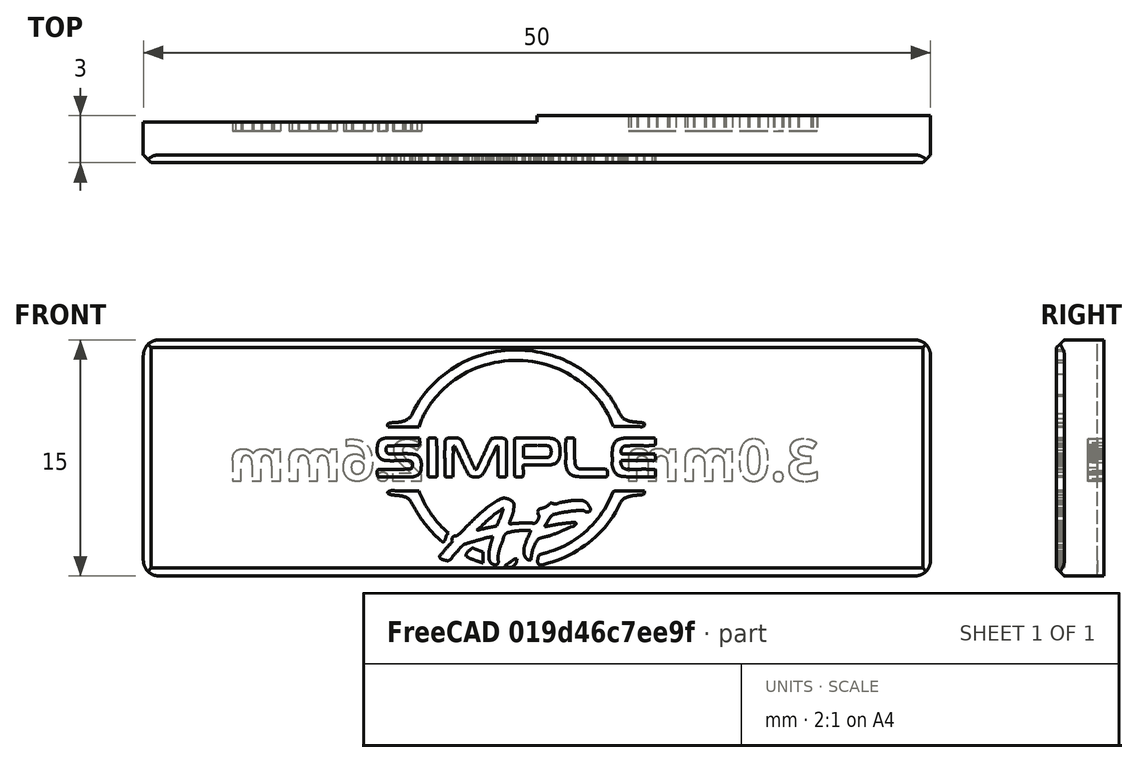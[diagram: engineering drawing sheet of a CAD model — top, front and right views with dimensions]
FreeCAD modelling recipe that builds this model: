
FCSTD DOCUMENT  (FreeCAD 26.3R20260630 (Git shallow))
Label: carto-measure
License: All rights reserved
LicenseURL: http://en.wikipedia.org/wiki/All_rights_reserved
objects: Sketcher::SketchObject×3, PartDesign::Pocket×2, App::Point×1, PartDesign::Pad×1, PartDesign::Chamfer×1, PartDesign::Fillet×1, PartDesign::Body×1
note: 22 computed .brp shape members not serialized (recipe doc carries the construction recipe); baked Part::Feature solids carry a one-line shape summary decoded from their .brp

FEATURE [App::Point] Origin001
  Role = Origin
FEATURE [Sketcher::SketchObject] Sketch
  ArcFitTolerance = 1e-06
  AttachmentSupport = -> [XY_Plane]
  ExternalTypes = [0]
  FullyConstrained = false
  MakeInternals = false
  MapMode = 5
  sketch-geometry (6):
    g0: LineSegment StartX=-28.082 StartY=2.6 StartZ=0 EndX=-3.08196 EndY=2.6 EndZ=0
    g1: LineSegment StartX=-3.08196 StartY=2.6 StartZ=0 EndX=-3.08196 EndY=3 EndZ=0
    g2: LineSegment StartX=-3.08196 StartY=3 StartZ=0 EndX=21.918 EndY=3 EndZ=0
    g3: LineSegment StartX=21.918 StartY=3 StartZ=0 EndX=21.918 EndY=0 EndZ=0
    g4: LineSegment StartX=21.918 StartY=0 StartZ=0 EndX=-28.082 EndY=0 EndZ=0
    g5: LineSegment StartX=-28.082 StartY=0 StartZ=0 EndX=-28.082 EndY=2.6 EndZ=0
  constraints (17):
    c: Horizontal(g0)
    c: Coincident(g0,g1)
    c: Vertical(g1)
    c: Coincident(g1,g2)
    c: Horizontal(g2)
    c: Coincident(g2,g3)
    c: PointOnObject(g3,g-1)
    c: Vertical(g3)
    c: Coincident(g3,g4)
    c: PointOnObject(g4,g-1)
    c: Coincident(g4,g5)
    c: Coincident(g5,g0)
    c: Vertical(g5)
    c: DistanceY(g5,g5) = 2.6
    c: DistanceY(g3,g3) = 3
    c: DistanceX(g4,g4) = 50
    c: DistanceX(g0,g0) = 25
FEATURE [PartDesign::Pad] Pad
  Direction = (0,0,1)
  FuzzyTolerance = 0
  Length = 15
  Length2 = 10
  Profile = -> Sketch
  ReferenceAxis = -> Sketch [N_Axis]
  SideType = 0
  Suppressed = false
  Type = 0
  Type2 = 0
FEATURE [Sketcher::SketchObject] Sketch001
  ArcFitTolerance = 1e-06
  AttachmentOffset = pos=(1,3.5,0) rot=(0,0,1;0rad)
  AttachmentSupport = -> [Pad]
  ExternalTypes = [0]
  FullyConstrained = false
  MakeInternals = true
  MapMode = 5
  Placement = pos=(1,8e-16,3.5) rot=(1,0,0;1.5708rad)
  sketch-geometry (160):
    g0: BSplineCurve PolesCount=4 KnotsCount=2 Degree=3 IsPeriodic=0
    g1: BSplineCurve PolesCount=4 KnotsCount=2 Degree=3 IsPeriodic=0
    g2: BSplineCurve PolesCount=4 KnotsCount=2 Degree=3 IsPeriodic=0
    g3: BSplineCurve PolesCount=4 KnotsCount=2 Degree=3 IsPeriodic=0
    g4: BSplineCurve PolesCount=4 KnotsCount=2 Degree=3 IsPeriodic=0
    g5: BSplineCurve PolesCount=4 KnotsCount=2 Degree=3 IsPeriodic=0
    g6: BSplineCurve PolesCount=4 KnotsCount=2 Degree=3 IsPeriodic=0
    g7: BSplineCurve PolesCount=4 KnotsCount=2 Degree=3 IsPeriodic=0
    g8: BSplineCurve PolesCount=4 KnotsCount=2 Degree=3 IsPeriodic=0
    g9: BSplineCurve PolesCount=4 KnotsCount=2 Degree=3 IsPeriodic=0
    g10: BSplineCurve PolesCount=4 KnotsCount=2 Degree=3 IsPeriodic=0
    g11: BSplineCurve PolesCount=4 KnotsCount=2 Degree=3 IsPeriodic=0
    g12: BSplineCurve PolesCount=4 KnotsCount=2 Degree=3 IsPeriodic=0
    g13: BSplineCurve PolesCount=4 KnotsCount=2 Degree=3 IsPeriodic=0
    g14: BSplineCurve PolesCount=4 KnotsCount=2 Degree=3 IsPeriodic=0
    g15: BSplineCurve PolesCount=4 KnotsCount=2 Degree=3 IsPeriodic=0
    g16: BSplineCurve PolesCount=4 KnotsCount=2 Degree=3 IsPeriodic=0
    g17: BSplineCurve PolesCount=4 KnotsCount=2 Degree=3 IsPeriodic=0
    g18: BSplineCurve PolesCount=4 KnotsCount=2 Degree=3 IsPeriodic=0
    g19: BSplineCurve PolesCount=4 KnotsCount=2 Degree=3 IsPeriodic=0
    g20: BSplineCurve PolesCount=4 KnotsCount=2 Degree=3 IsPeriodic=0
    g21: BSplineCurve PolesCount=4 KnotsCount=2 Degree=3 IsPeriodic=0
    g22: BSplineCurve PolesCount=4 KnotsCount=2 Degree=3 IsPeriodic=0
    g23: BSplineCurve PolesCount=4 KnotsCount=2 Degree=3 IsPeriodic=0
    g24: BSplineCurve PolesCount=4 KnotsCount=2 Degree=3 IsPeriodic=0
    g25: BSplineCurve PolesCount=4 KnotsCount=2 Degree=3 IsPeriodic=0
    g26: BSplineCurve PolesCount=4 KnotsCount=2 Degree=3 IsPeriodic=0
    g27: BSplineCurve PolesCount=4 KnotsCount=2 Degree=3 IsPeriodic=0
    g28: BSplineCurve PolesCount=4 KnotsCount=2 Degree=3 IsPeriodic=0
    g29: BSplineCurve PolesCount=4 KnotsCount=2 Degree=3 IsPeriodic=0
    g30: BSplineCurve PolesCount=4 KnotsCount=2 Degree=3 IsPeriodic=0
    g31: BSplineCurve PolesCount=4 KnotsCount=2 Degree=3 IsPeriodic=0
    g32: BSplineCurve PolesCount=4 KnotsCount=2 Degree=3 IsPeriodic=0
    g33: BSplineCurve PolesCount=4 KnotsCount=2 Degree=3 IsPeriodic=0
    g34: BSplineCurve PolesCount=4 KnotsCount=2 Degree=3 IsPeriodic=0
    g35: BSplineCurve PolesCount=4 KnotsCount=2 Degree=3 IsPeriodic=0
    g36: BSplineCurve PolesCount=4 KnotsCount=2 Degree=3 IsPeriodic=0
    g37: BSplineCurve PolesCount=4 KnotsCount=2 Degree=3 IsPeriodic=0
    g38: BSplineCurve PolesCount=4 KnotsCount=2 Degree=3 IsPeriodic=0
    g39: BSplineCurve PolesCount=4 KnotsCount=2 Degree=3 IsPeriodic=0
    g40: BSplineCurve PolesCount=4 KnotsCount=2 Degree=3 IsPeriodic=0
    g41: BSplineCurve PolesCount=4 KnotsCount=2 Degree=3 IsPeriodic=0
    g42: BSplineCurve PolesCount=4 KnotsCount=2 Degree=3 IsPeriodic=0
    g43: BSplineCurve PolesCount=4 KnotsCount=2 Degree=3 IsPeriodic=0
    g44: BSplineCurve PolesCount=4 KnotsCount=2 Degree=3 IsPeriodic=0
    g45: BSplineCurve PolesCount=4 KnotsCount=2 Degree=3 IsPeriodic=0
    g46: BSplineCurve PolesCount=4 KnotsCount=2 Degree=3 IsPeriodic=0
    g47: BSplineCurve PolesCount=4 KnotsCount=2 Degree=3 IsPeriodic=0
    g48: BSplineCurve PolesCount=4 KnotsCount=2 Degree=3 IsPeriodic=0
    g49: BSplineCurve PolesCount=4 KnotsCount=2 Degree=3 IsPeriodic=0
    g50: BSplineCurve PolesCount=4 KnotsCount=2 Degree=3 IsPeriodic=0
    g51: BSplineCurve PolesCount=4 KnotsCount=2 Degree=3 IsPeriodic=0
    g52: BSplineCurve PolesCount=4 KnotsCount=2 Degree=3 IsPeriodic=0
    g53: BSplineCurve PolesCount=4 KnotsCount=2 Degree=3 IsPeriodic=0
    g54: BSplineCurve PolesCount=4 KnotsCount=2 Degree=3 IsPeriodic=0
    g55: BSplineCurve PolesCount=4 KnotsCount=2 Degree=3 IsPeriodic=0
    g56: BSplineCurve PolesCount=4 KnotsCount=2 Degree=3 IsPeriodic=0
    g57: BSplineCurve PolesCount=4 KnotsCount=2 Degree=3 IsPeriodic=0
    g58: BSplineCurve PolesCount=4 KnotsCount=2 Degree=3 IsPeriodic=0
    g59: BSplineCurve PolesCount=4 KnotsCount=2 Degree=3 IsPeriodic=0
    g60: BSplineCurve PolesCount=4 KnotsCount=2 Degree=3 IsPeriodic=0
    g61: BSplineCurve PolesCount=4 KnotsCount=2 Degree=3 IsPeriodic=0
    g62: BSplineCurve PolesCount=4 KnotsCount=2 Degree=3 IsPeriodic=0
    g63: BSplineCurve PolesCount=4 KnotsCount=2 Degree=3 IsPeriodic=0
    g64: BSplineCurve PolesCount=4 KnotsCount=2 Degree=3 IsPeriodic=0
    g65: BSplineCurve PolesCount=4 KnotsCount=2 Degree=3 IsPeriodic=0
    g66: BSplineCurve PolesCount=4 KnotsCount=2 Degree=3 IsPeriodic=0
    g67: BSplineCurve PolesCount=4 KnotsCount=2 Degree=3 IsPeriodic=0
    g68: BSplineCurve PolesCount=4 KnotsCount=2 Degree=3 IsPeriodic=0
    g69: BSplineCurve PolesCount=4 KnotsCount=2 Degree=3 IsPeriodic=0
    g70: BSplineCurve PolesCount=4 KnotsCount=2 Degree=3 IsPeriodic=0
    g71: BSplineCurve PolesCount=4 KnotsCount=2 Degree=3 IsPeriodic=0
    g72: BSplineCurve PolesCount=4 KnotsCount=2 Degree=3 IsPeriodic=0
    g73: BSplineCurve PolesCount=4 KnotsCount=2 Degree=3 IsPeriodic=0
    g74: BSplineCurve PolesCount=4 KnotsCount=2 Degree=3 IsPeriodic=0
    g75: BSplineCurve PolesCount=4 KnotsCount=2 Degree=3 IsPeriodic=0
    g76: BSplineCurve PolesCount=4 KnotsCount=2 Degree=3 IsPeriodic=0
    g77: BSplineCurve PolesCount=4 KnotsCount=2 Degree=3 IsPeriodic=0
    g78: BSplineCurve PolesCount=4 KnotsCount=2 Degree=3 IsPeriodic=0
    g79: BSplineCurve PolesCount=4 KnotsCount=2 Degree=3 IsPeriodic=0
    g80: BSplineCurve PolesCount=4 KnotsCount=2 Degree=3 IsPeriodic=0
    g81: BSplineCurve PolesCount=4 KnotsCount=2 Degree=3 IsPeriodic=0
    g82: BSplineCurve PolesCount=4 KnotsCount=2 Degree=3 IsPeriodic=0
    g83: BSplineCurve PolesCount=4 KnotsCount=2 Degree=3 IsPeriodic=0
    g84: BSplineCurve PolesCount=4 KnotsCount=2 Degree=3 IsPeriodic=0
    g85: BSplineCurve PolesCount=4 KnotsCount=2 Degree=3 IsPeriodic=0
    g86: BSplineCurve PolesCount=4 KnotsCount=2 Degree=3 IsPeriodic=0
    g87: BSplineCurve PolesCount=4 KnotsCount=2 Degree=3 IsPeriodic=0
    g88: BSplineCurve PolesCount=4 KnotsCount=2 Degree=3 IsPeriodic=0
    g89: BSplineCurve PolesCount=4 KnotsCount=2 Degree=3 IsPeriodic=0
    g90: BSplineCurve PolesCount=4 KnotsCount=2 Degree=3 IsPeriodic=0
    g91: BSplineCurve PolesCount=4 KnotsCount=2 Degree=3 IsPeriodic=0
    g92: BSplineCurve PolesCount=4 KnotsCount=2 Degree=3 IsPeriodic=0
    g93: BSplineCurve PolesCount=4 KnotsCount=2 Degree=3 IsPeriodic=0
    g94: BSplineCurve PolesCount=4 KnotsCount=2 Degree=3 IsPeriodic=0
    g95: BSplineCurve PolesCount=4 KnotsCount=2 Degree=3 IsPeriodic=0
    g96: BSplineCurve PolesCount=4 KnotsCount=2 Degree=3 IsPeriodic=0
    g97: BSplineCurve PolesCount=4 KnotsCount=2 Degree=3 IsPeriodic=0
    g98: BSplineCurve PolesCount=4 KnotsCount=2 Degree=3 IsPeriodic=0
    g99: BSplineCurve PolesCount=4 KnotsCount=2 Degree=3 IsPeriodic=0
    g100: BSplineCurve PolesCount=4 KnotsCount=2 Degree=3 IsPeriodic=0
    g101: BSplineCurve PolesCount=4 KnotsCount=2 Degree=3 IsPeriodic=0
    g102: BSplineCurve PolesCount=4 KnotsCount=2 Degree=3 IsPeriodic=0
    g103: BSplineCurve PolesCount=4 KnotsCount=2 Degree=3 IsPeriodic=0
    g104: BSplineCurve PolesCount=4 KnotsCount=2 Degree=3 IsPeriodic=0
    g105: BSplineCurve PolesCount=2 KnotsCount=2 Degree=1 IsPeriodic=0
    g106: BSplineCurve PolesCount=4 KnotsCount=2 Degree=3 IsPeriodic=0
    g107: BSplineCurve PolesCount=4 KnotsCount=2 Degree=3 IsPeriodic=0
    g108: BSplineCurve PolesCount=4 KnotsCount=2 Degree=3 IsPeriodic=0
    g109: BSplineCurve PolesCount=4 KnotsCount=2 Degree=3 IsPeriodic=0
    g110: BSplineCurve PolesCount=4 KnotsCount=2 Degree=3 IsPeriodic=0
    g111: BSplineCurve PolesCount=4 KnotsCount=2 Degree=3 IsPeriodic=0
    g112: BSplineCurve PolesCount=4 KnotsCount=2 Degree=3 IsPeriodic=0
    g113: BSplineCurve PolesCount=4 KnotsCount=2 Degree=3 IsPeriodic=0
    g114: BSplineCurve PolesCount=4 KnotsCount=2 Degree=3 IsPeriodic=0
    g115: BSplineCurve PolesCount=4 KnotsCount=2 Degree=3 IsPeriodic=0
    g116: BSplineCurve PolesCount=4 KnotsCount=2 Degree=3 IsPeriodic=0
    g117: BSplineCurve PolesCount=4 KnotsCount=2 Degree=3 IsPeriodic=0
    g118: BSplineCurve PolesCount=4 KnotsCount=2 Degree=3 IsPeriodic=0
    g119: BSplineCurve PolesCount=4 KnotsCount=2 Degree=3 IsPeriodic=0
    g120: BSplineCurve PolesCount=4 KnotsCount=2 Degree=3 IsPeriodic=0
    g121: BSplineCurve PolesCount=4 KnotsCount=2 Degree=3 IsPeriodic=0
    g122: BSplineCurve PolesCount=4 KnotsCount=2 Degree=3 IsPeriodic=0
    g123: BSplineCurve PolesCount=4 KnotsCount=2 Degree=3 IsPeriodic=0
    g124: BSplineCurve PolesCount=4 KnotsCount=2 Degree=3 IsPeriodic=0
    g125: BSplineCurve PolesCount=4 KnotsCount=2 Degree=3 IsPeriodic=0
    g126: BSplineCurve PolesCount=4 KnotsCount=2 Degree=3 IsPeriodic=0
    g127: BSplineCurve PolesCount=4 KnotsCount=2 Degree=3 IsPeriodic=0
    g128: BSplineCurve PolesCount=4 KnotsCount=2 Degree=3 IsPeriodic=0
    g129: BSplineCurve PolesCount=4 KnotsCount=2 Degree=3 IsPeriodic=0
    g130: BSplineCurve PolesCount=4 KnotsCount=2 Degree=3 IsPeriodic=0
    g131: BSplineCurve PolesCount=4 KnotsCount=2 Degree=3 IsPeriodic=0
    g132: BSplineCurve PolesCount=4 KnotsCount=2 Degree=3 IsPeriodic=0
    g133: BSplineCurve PolesCount=4 KnotsCount=2 Degree=3 IsPeriodic=0
    g134: BSplineCurve PolesCount=4 KnotsCount=2 Degree=3 IsPeriodic=0
    g135: BSplineCurve PolesCount=4 KnotsCount=2 Degree=3 IsPeriodic=0
    g136: BSplineCurve PolesCount=4 KnotsCount=2 Degree=3 IsPeriodic=0
    g137: BSplineCurve PolesCount=4 KnotsCount=2 Degree=3 IsPeriodic=0
    g138: BSplineCurve PolesCount=4 KnotsCount=2 Degree=3 IsPeriodic=0
    g139: BSplineCurve PolesCount=4 KnotsCount=2 Degree=3 IsPeriodic=0
    g140: BSplineCurve PolesCount=4 KnotsCount=2 Degree=3 IsPeriodic=0
    g141: BSplineCurve PolesCount=4 KnotsCount=2 Degree=3 IsPeriodic=0
    g142: BSplineCurve PolesCount=4 KnotsCount=2 Degree=3 IsPeriodic=0
    g143: BSplineCurve PolesCount=4 KnotsCount=2 Degree=3 IsPeriodic=0
    g144: BSplineCurve PolesCount=4 KnotsCount=2 Degree=3 IsPeriodic=0
    g145: BSplineCurve PolesCount=4 KnotsCount=2 Degree=3 IsPeriodic=0
    g146: BSplineCurve PolesCount=4 KnotsCount=2 Degree=3 IsPeriodic=0
    g147: BSplineCurve PolesCount=4 KnotsCount=2 Degree=3 IsPeriodic=0
    g148: BSplineCurve PolesCount=4 KnotsCount=2 Degree=3 IsPeriodic=0
    g149: BSplineCurve PolesCount=4 KnotsCount=2 Degree=3 IsPeriodic=0
    g150: BSplineCurve PolesCount=4 KnotsCount=2 Degree=3 IsPeriodic=0
    g151: BSplineCurve PolesCount=4 KnotsCount=2 Degree=3 IsPeriodic=0
    g152: BSplineCurve PolesCount=4 KnotsCount=2 Degree=3 IsPeriodic=0
    g153: BSplineCurve PolesCount=4 KnotsCount=2 Degree=3 IsPeriodic=0
    g154: BSplineCurve PolesCount=4 KnotsCount=2 Degree=3 IsPeriodic=0
    g155: BSplineCurve PolesCount=4 KnotsCount=2 Degree=3 IsPeriodic=0
    g156: BSplineCurve PolesCount=4 KnotsCount=2 Degree=3 IsPeriodic=0
    g157: BSplineCurve PolesCount=4 KnotsCount=2 Degree=3 IsPeriodic=0
    g158: BSplineCurve PolesCount=4 KnotsCount=2 Degree=3 IsPeriodic=0
    g159: BSplineCurve PolesCount=4 KnotsCount=2 Degree=3 IsPeriodic=0
  constraints (160):
    c: Coincident(g117,g118)
    c: Coincident(g118,g119)
    c: Coincident(g108,g109)
    c: Coincident(g107,g108)
    c: Coincident(g112,g113)
    c: Coincident(g7,g8)
    c: Coincident(g156,g157)
    c: Coincident(g113,g114)
    c: Coincident(g8,g9)
    c: Coincident(g157,g158)
    c: Coincident(g109,g110)
    c: Coincident(g116,g117)
    c: Coincident(g106,g107)
    c: Coincident(g155,g156)
    c: Coincident(g119,g120)
    c: Coincident(g106,g120)
    c: Coincident(g9,g10)
    c: Coincident(g114,g115)
    c: Coincident(g158,g159)
    c: Coincident(g6,g7)
    c: Coincident(g111,g112)
    c: Coincident(g110,g111)
    c: Coincident(g115,g116)
    c: Coincident(g102,g103)
    c: Coincident(g101,g102)
    c: Coincident(g101,g105)
    c: Coincident(g154,g155)
    c: Coincident(g103,g104)
    c: Coincident(g104,g105)
    c: Coincident(g5,g6)
    c: Coincident(g61,g62)
    c: Coincident(g153,g154)
    c: Coincident(g94,g95)
    c: Coincident(g95,g96)
    c: Coincident(g62,g63)
    c: Coincident(g153,g159)
    c: Coincident(g93,g94)
    c: Coincident(g60,g61)
    c: Coincident(g92,g93)
    c: Coincident(g91,g92)
    c: Coincident(g63,g64)
    c: Coincident(g59,g60)
    c: Coincident(g96,g97)
    c: Coincident(g64,g65)
    c: Coincident(g65,g66)
    c: Coincident(g143,g144)
    c: Coincident(g97,g98)
    c: Coincident(g58,g59)
    c: Coincident(g90,g91)
    c: Coincident(g141,g144)
    c: Coincident(g98,g99)
    c: Coincident(g125,g126)
    c: Coincident(g121,g126)
    c: Coincident(g99,g100)
    c: Coincident(g89,g90)
    c: Coincident(g141,g142)
    c: Coincident(g82,g100)
    c: Coincident(g142,g143)
    c: Coincident(g66,g67)
    c: Coincident(g124,g125)
    c: Coincident(g69,g70)
    c: Coincident(g68,g69)
    c: Coincident(g82,g83)
    c: Coincident(g67,g68)
    c: Coincident(g88,g89)
    c: Coincident(g123,g124)
    c: Coincident(g121,g122)
    c: Coincident(g87,g88)
    c: Coincident(g86,g87)
    c: Coincident(g70,g71)
    c: Coincident(g57,g58)
    c: Coincident(g71,g72)
    c: Coincident(g10,g11)
    c: Coincident(g31,g72)
    c: Coincident(g122,g123)
    c: Coincident(g83,g84)
    c: Coincident(g84,g85)
    c: Coincident(g85,g86)
    c: Coincident(g27,g28)
    c: Coincident(g28,g29)
    c: Coincident(g31,g32)
    c: Coincident(g53,g54)
    c: Coincident(g56,g57)
    c: Coincident(g54,g55)
    c: Coincident(g52,g53)
    c: Coincident(g55,g56)
    c: Coincident(g78,g79)
    c: Coincident(g77,g78)
    c: Coincident(g27,g30)
    c: Coincident(g29,g30)
    c: Coincident(g76,g77)
    c: Coincident(g75,g76)
    c: Coincident(g128,g129)
    c: Coincident(g127,g128)
    c: Coincident(g33,g34)
    c: Coincident(g34,g35)
    c: Coincident(g79,g80)
    c: Coincident(g32,g33)
    c: Coincident(g35,g36)
    c: Coincident(g51,g52)
    c: Coincident(g127,g131)
    c: Coincident(g4,g5)
    c: Coincident(g36,g37)
    c: Coincident(g145,g152)
    c: Coincident(g50,g51)
    c: Coincident(g74,g75)
    c: Coincident(g151,g152)
    c: Coincident(g49,g50)
    c: Coincident(g41,g42)
    c: Coincident(g129,g130)
    c: Coincident(g130,g131)
    c: Coincident(g145,g146)
    c: Coincident(g48,g49)
    c: Coincident(g42,g43)
    c: Coincident(g80,g81)
    c: Coincident(g37,g38)
    c: Coincident(g73,g81)
    c: Coincident(g73,g74)
    c: Coincident(g47,g48)
    c: Coincident(g135,g136)
    c: Coincident(g136,g137)
    c: Coincident(g38,g39)
    c: Coincident(g39,g40)
    c: Coincident(g40,g41)
    c: Coincident(g134,g135)
    c: Coincident(g137,g138)
    c: Coincident(g138,g139)
    c: Coincident(g46,g47)
    c: Coincident(g43,g44)
    c: Coincident(g11,g12)
    c: Coincident(g45,g46)
    c: Coincident(g44,g45)
    c: Coincident(g139,g140)
    c: Coincident(g132,g140)
    c: Coincident(g133,g134)
    c: Coincident(g132,g133)
    c: Coincident(g0,g12)
    c: Coincident(g24,g25)
    c: Coincident(g146,g147)
    c: Coincident(g3,g4)
    c: Coincident(g25,g26)
    c: Coincident(g150,g151)
    c: Coincident(g19,g20)
    c: Coincident(g16,g17)
    c: Coincident(g23,g24)
    c: Coincident(g0,g1)
    c: Coincident(g15,g16)
    c: Coincident(g13,g26)
    c: Coincident(g147,g148)
    c: Coincident(g20,g21)
    c: Coincident(g2,g3)
    c: Coincident(g149,g150)
    c: Coincident(g1,g2)
    c: Coincident(g148,g149)
    c: Coincident(g18,g19)
    c: Coincident(g22,g23)
    c: Coincident(g14,g15)
    c: Coincident(g17,g18)
    c: Coincident(g21,g22)
    c: Coincident(g13,g14)
FEATURE [PartDesign::Pocket] Pocket
  BaseFeature = -> Pad
  Direction = (0,1,-2e-16)
  FuzzyTolerance = 0
  Length = 0.5
  Length2 = 5
  Profile = -> Sketch001
  ReferenceAxis = -> Sketch001 [N_Axis]
  Refine = true
  SideType = 0
  Suppressed = false
  Type = 0
  Type2 = 0
FEATURE [PartDesign::Chamfer] Chamfer
  Angle = 45
  Base = -> Pocket [Edge13,Edge16,Edge17,Edge5]
  BaseFeature = -> Pocket
  ChamferType = 0
  FlipDirection = false
  FuzzyTolerance = 0
  Refine = true
  Size = 0.5
  Size2 = 1
  SupportTransform = false
  Suppressed = false
  UseAllEdges = false
FEATURE [PartDesign::Fillet] Fillet
  Base = -> Chamfer [Edge5,Edge1,Edge4,Edge15]
  BaseFeature = -> Chamfer
  FuzzyTolerance = 0
  Radius = 1
  Refine = true
  SupportTransform = false
  Suppressed = false
  UseAllEdges = false
FEATURE [Sketcher::SketchObject] Sketch002
  ArcFitTolerance = 1e-06
  AttachmentSupport = -> [Fillet]
  ExternalTypes = [0]
  FullyConstrained = false
  MakeInternals = true
  MapMode = 5
  Placement = pos=(0,3,0) rot=(0,0.707107,0.707107;3.14159rad)
  sketch-geometry (222):
    g0: LineSegment [constr] StartX=-14.7202 StartY=6 StartZ=0 EndX=-2.72016 EndY=6 EndZ=0
    g1: LineSegment [constr] StartX=10.4105 StartY=6 StartZ=0 EndX=22.4105 EndY=6 EndZ=0
    g2: BSplineCurve PolesCount=3 KnotsCount=2 Degree=2 IsPeriodic=0
    g3: BSplineCurve PolesCount=3 KnotsCount=2 Degree=2 IsPeriodic=0
    g4: LineSegment StartX=-13.5529 StartY=7.4247 StartZ=0 EndX=-13.5529 EndY=7.41397 EndZ=0
    g5: BSplineCurve PolesCount=3 KnotsCount=2 Degree=2 IsPeriodic=0
    g6: BSplineCurve PolesCount=3 KnotsCount=2 Degree=2 IsPeriodic=0
    g7: BSplineCurve PolesCount=3 KnotsCount=2 Degree=2 IsPeriodic=0
    g8: BSplineCurve PolesCount=3 KnotsCount=2 Degree=2 IsPeriodic=0
    g9: BSplineCurve PolesCount=3 KnotsCount=2 Degree=2 IsPeriodic=0
    g10: LineSegment StartX=-14.7202 StartY=6.15373 StartZ=0 EndX=-14.7202 EndY=6.62386 EndZ=0
    g11: BSplineCurve PolesCount=3 KnotsCount=2 Degree=2 IsPeriodic=0
    g12: BSplineCurve PolesCount=3 KnotsCount=2 Degree=2 IsPeriodic=0
    g13: BSplineCurve PolesCount=3 KnotsCount=2 Degree=2 IsPeriodic=0
    g14: BSplineCurve PolesCount=3 KnotsCount=2 Degree=2 IsPeriodic=0
    g15: BSplineCurve PolesCount=3 KnotsCount=2 Degree=2 IsPeriodic=0
    g16: BSplineCurve PolesCount=3 KnotsCount=2 Degree=2 IsPeriodic=0
    g17: LineSegment StartX=-14.1195 StartY=7.1798 StartZ=0 EndX=-14.318 EndY=7.1798 EndZ=0
    g18: LineSegment StartX=-14.318 StartY=7.1798 StartZ=0 EndX=-14.318 EndY=7.60346 EndZ=0
    g19: LineSegment StartX=-14.318 StartY=7.60346 StartZ=0 EndX=-14.116 EndY=7.60346 EndZ=0
    g20: BSplineCurve PolesCount=3 KnotsCount=2 Degree=2 IsPeriodic=0
    g21: BSplineCurve PolesCount=3 KnotsCount=2 Degree=2 IsPeriodic=0
    g22: BSplineCurve PolesCount=3 KnotsCount=2 Degree=2 IsPeriodic=0
    g23: BSplineCurve PolesCount=3 KnotsCount=2 Degree=2 IsPeriodic=0
    g24: BSplineCurve PolesCount=3 KnotsCount=2 Degree=2 IsPeriodic=0
    g25: LineSegment StartX=-14.461 StartY=8.06108 StartZ=0 EndX=-14.7166 EndY=8.44183 EndZ=0
    g26: BSplineCurve PolesCount=3 KnotsCount=2 Degree=2 IsPeriodic=0
    g27: BSplineCurve PolesCount=3 KnotsCount=2 Degree=2 IsPeriodic=0
    g28: BSplineCurve PolesCount=3 KnotsCount=2 Degree=2 IsPeriodic=0
    g29: BSplineCurve PolesCount=3 KnotsCount=2 Degree=2 IsPeriodic=0
    g30: BSplineCurve PolesCount=3 KnotsCount=2 Degree=2 IsPeriodic=0
    g31: BSplineCurve PolesCount=3 KnotsCount=2 Degree=2 IsPeriodic=0
    g32: BSplineCurve PolesCount=3 KnotsCount=2 Degree=2 IsPeriodic=0
    g33: BSplineCurve PolesCount=3 KnotsCount=2 Degree=2 IsPeriodic=0
    g34: BSplineCurve PolesCount=3 KnotsCount=2 Degree=2 IsPeriodic=0
    g35: BSplineCurve PolesCount=3 KnotsCount=2 Degree=2 IsPeriodic=0
    g36: BSplineCurve PolesCount=3 KnotsCount=2 Degree=2 IsPeriodic=0
    g37: BSplineCurve PolesCount=3 KnotsCount=2 Degree=2 IsPeriodic=0
    g38: BSplineCurve PolesCount=3 KnotsCount=2 Degree=2 IsPeriodic=0
    g39: BSplineCurve PolesCount=3 KnotsCount=2 Degree=2 IsPeriodic=0
    g40: BSplineCurve PolesCount=3 KnotsCount=2 Degree=2 IsPeriodic=0
    g41: BSplineCurve PolesCount=3 KnotsCount=2 Degree=2 IsPeriodic=0
    g42: BSplineCurve PolesCount=3 KnotsCount=2 Degree=2 IsPeriodic=0
    g43: BSplineCurve PolesCount=3 KnotsCount=2 Degree=2 IsPeriodic=0
    g44: BSplineCurve PolesCount=3 KnotsCount=2 Degree=2 IsPeriodic=0
    g45: BSplineCurve PolesCount=3 KnotsCount=2 Degree=2 IsPeriodic=0
    g46: BSplineCurve PolesCount=3 KnotsCount=2 Degree=2 IsPeriodic=0
    g47: BSplineCurve PolesCount=3 KnotsCount=2 Degree=2 IsPeriodic=0
    g48: BSplineCurve PolesCount=3 KnotsCount=2 Degree=2 IsPeriodic=0
    g49: BSplineCurve PolesCount=3 KnotsCount=2 Degree=2 IsPeriodic=0
    g50: BSplineCurve PolesCount=3 KnotsCount=2 Degree=2 IsPeriodic=0
    g51: BSplineCurve PolesCount=3 KnotsCount=2 Degree=2 IsPeriodic=0
    g52: BSplineCurve PolesCount=3 KnotsCount=2 Degree=2 IsPeriodic=0
    g53: LineSegment StartX=-7.56092 StartY=6.04826 StartZ=0 EndX=-8.10613 EndY=6.04826 EndZ=0
    g54: LineSegment StartX=-8.10613 StartY=6.04826 StartZ=0 EndX=-8.10613 EndY=7.21555 EndZ=0
    g55: BSplineCurve PolesCount=3 KnotsCount=2 Degree=2 IsPeriodic=0
    g56: BSplineCurve PolesCount=3 KnotsCount=2 Degree=2 IsPeriodic=0
    g57: BSplineCurve PolesCount=3 KnotsCount=2 Degree=2 IsPeriodic=0
    g58: BSplineCurve PolesCount=3 KnotsCount=2 Degree=2 IsPeriodic=0
    g59: LineSegment StartX=-8.80507 StartY=6.98853 StartZ=0 EndX=-8.80507 EndY=6.04826 EndZ=0
    g60: LineSegment StartX=-8.80507 StartY=6.04826 StartZ=0 EndX=-9.35028 EndY=6.04826 EndZ=0
    g61: LineSegment StartX=-9.35028 StartY=6.04826 StartZ=0 EndX=-9.35028 EndY=8.04678 EndZ=0
    g62: LineSegment StartX=-9.35028 StartY=8.04678 StartZ=0 EndX=-8.93378 EndY=8.04678 EndZ=0
    g63: LineSegment StartX=-8.93378 StartY=8.04678 StartZ=0 EndX=-8.86048 EndY=7.79115 EndZ=0
    g64: LineSegment StartX=-8.86048 StartY=7.79115 StartZ=0 EndX=-8.8301 EndY=7.79115 EndZ=0
    g65: BSplineCurve PolesCount=3 KnotsCount=2 Degree=2 IsPeriodic=0
    g66: BSplineCurve PolesCount=3 KnotsCount=2 Degree=2 IsPeriodic=0
    g67: BSplineCurve PolesCount=3 KnotsCount=2 Degree=2 IsPeriodic=0
    g68: LineSegment StartX=-7.64136 StartY=7.79115 StartZ=0 EndX=-7.59309 EndY=7.79115 EndZ=0
    g69: BSplineCurve PolesCount=3 KnotsCount=2 Degree=2 IsPeriodic=0
    g70: BSplineCurve PolesCount=3 KnotsCount=2 Degree=2 IsPeriodic=0
    g71: BSplineCurve PolesCount=3 KnotsCount=2 Degree=2 IsPeriodic=0
    g72: BSplineCurve PolesCount=3 KnotsCount=2 Degree=2 IsPeriodic=0
    g73: LineSegment StartX=-6.31498 StartY=7.35141 StartZ=0 EndX=-6.31498 EndY=6.04826 EndZ=0
    g74: LineSegment StartX=-6.31498 StartY=6.04826 StartZ=0 EndX=-6.86197 EndY=6.04826 EndZ=0
    g75: LineSegment StartX=-6.86197 StartY=6.04826 StartZ=0 EndX=-6.86197 EndY=7.21555 EndZ=0
    g76: BSplineCurve PolesCount=3 KnotsCount=2 Degree=2 IsPeriodic=0
    g77: BSplineCurve PolesCount=3 KnotsCount=2 Degree=2 IsPeriodic=0
    g78: BSplineCurve PolesCount=3 KnotsCount=2 Degree=2 IsPeriodic=0
    g79: BSplineCurve PolesCount=3 KnotsCount=2 Degree=2 IsPeriodic=0
    g80: LineSegment StartX=-7.56092 StartY=7.0511 StartZ=0 EndX=-7.56092 EndY=6.04826 EndZ=0
    g81: LineSegment StartX=-3.9661 StartY=6.04826 StartZ=0 EndX=-4.51131 EndY=6.04826 EndZ=0
    g82: LineSegment StartX=-4.51131 StartY=6.04826 StartZ=0 EndX=-4.51131 EndY=7.21555 EndZ=0
    g83: BSplineCurve PolesCount=3 KnotsCount=2 Degree=2 IsPeriodic=0
    g84: BSplineCurve PolesCount=3 KnotsCount=2 Degree=2 IsPeriodic=0
    g85: BSplineCurve PolesCount=3 KnotsCount=2 Degree=2 IsPeriodic=0
    g86: BSplineCurve PolesCount=3 KnotsCount=2 Degree=2 IsPeriodic=0
    g87: LineSegment StartX=-5.21025 StartY=6.98853 StartZ=0 EndX=-5.21025 EndY=6.04826 EndZ=0
    g88: LineSegment StartX=-5.21025 StartY=6.04826 StartZ=0 EndX=-5.75546 EndY=6.04826 EndZ=0
    g89: LineSegment StartX=-5.75546 StartY=6.04826 StartZ=0 EndX=-5.75546 EndY=8.04678 EndZ=0
    g90: LineSegment StartX=-5.75546 StartY=8.04678 StartZ=0 EndX=-5.33896 EndY=8.04678 EndZ=0
    g91: LineSegment StartX=-5.33896 StartY=8.04678 StartZ=0 EndX=-5.26567 EndY=7.79115 EndZ=0
    g92: LineSegment StartX=-5.26567 StartY=7.79115 StartZ=0 EndX=-5.23528 EndY=7.79115 EndZ=0
    g93: BSplineCurve PolesCount=3 KnotsCount=2 Degree=2 IsPeriodic=0
    g94: BSplineCurve PolesCount=3 KnotsCount=2 Degree=2 IsPeriodic=0
    g95: BSplineCurve PolesCount=3 KnotsCount=2 Degree=2 IsPeriodic=0
    g96: LineSegment StartX=-4.04654 StartY=7.79115 StartZ=0 EndX=-3.99828 EndY=7.79115 EndZ=0
    g97: BSplineCurve PolesCount=3 KnotsCount=2 Degree=2 IsPeriodic=0
    g98: BSplineCurve PolesCount=3 KnotsCount=2 Degree=2 IsPeriodic=0
    g99: BSplineCurve PolesCount=3 KnotsCount=2 Degree=2 IsPeriodic=0
    g100: BSplineCurve PolesCount=3 KnotsCount=2 Degree=2 IsPeriodic=0
    g101: LineSegment StartX=-2.72016 StartY=7.35141 StartZ=0 EndX=-2.72016 EndY=6.04826 EndZ=0
    g102: LineSegment StartX=-2.72016 StartY=6.04826 StartZ=0 EndX=-3.26716 EndY=6.04826 EndZ=0
    g103: LineSegment StartX=-3.26716 StartY=6.04826 StartZ=0 EndX=-3.26716 EndY=7.21555 EndZ=0
    g104: BSplineCurve PolesCount=3 KnotsCount=2 Degree=2 IsPeriodic=0
    g105: BSplineCurve PolesCount=3 KnotsCount=2 Degree=2 IsPeriodic=0
    g106: BSplineCurve PolesCount=3 KnotsCount=2 Degree=2 IsPeriodic=0
    g107: BSplineCurve PolesCount=3 KnotsCount=2 Degree=2 IsPeriodic=0
    g108: LineSegment StartX=-3.9661 StartY=7.0511 StartZ=0 EndX=-3.9661 EndY=6.04826 EndZ=0
    g109: LineSegment StartX=12.2446 StartY=6.04826 StartZ=0 EndX=10.4177 EndY=6.04826 EndZ=0
    g110: LineSegment StartX=10.4177 StartY=6.04826 StartZ=0 EndX=10.4177 EndY=6.43259 EndZ=0
    g111: LineSegment StartX=10.4177 StartY=6.43259 StartZ=0 EndX=11.0737 EndY=7.09578 EndZ=0
    g112: BSplineCurve PolesCount=3 KnotsCount=2 Degree=2 IsPeriodic=0
    g113: BSplineCurve PolesCount=3 KnotsCount=2 Degree=2 IsPeriodic=0
    g114: BSplineCurve PolesCount=3 KnotsCount=2 Degree=2 IsPeriodic=0
    g115: BSplineCurve PolesCount=3 KnotsCount=2 Degree=2 IsPeriodic=0
    g116: BSplineCurve PolesCount=3 KnotsCount=2 Degree=2 IsPeriodic=0
    g117: BSplineCurve PolesCount=3 KnotsCount=2 Degree=2 IsPeriodic=0
    g118: BSplineCurve PolesCount=3 KnotsCount=2 Degree=2 IsPeriodic=0
    g119: LineSegment StartX=10.7108 StartY=7.96991 StartZ=0 EndX=10.4105 EndY=8.32564 EndZ=0
    g120: BSplineCurve PolesCount=3 KnotsCount=2 Degree=2 IsPeriodic=0
    g121: BSplineCurve PolesCount=3 KnotsCount=2 Degree=2 IsPeriodic=0
    g122: BSplineCurve PolesCount=3 KnotsCount=2 Degree=2 IsPeriodic=0
    g123: BSplineCurve PolesCount=3 KnotsCount=2 Degree=2 IsPeriodic=0
    g124: BSplineCurve PolesCount=3 KnotsCount=2 Degree=2 IsPeriodic=0
    g125: BSplineCurve PolesCount=3 KnotsCount=2 Degree=2 IsPeriodic=0
    g126: BSplineCurve PolesCount=3 KnotsCount=2 Degree=2 IsPeriodic=0
    g127: BSplineCurve PolesCount=3 KnotsCount=2 Degree=2 IsPeriodic=0
    g128: BSplineCurve PolesCount=3 KnotsCount=2 Degree=2 IsPeriodic=0
    g129: LineSegment StartX=11.4419 StartY=6.85446 StartZ=0 EndX=11.1059 EndY=6.53806 EndZ=0
    g130: LineSegment StartX=11.1059 StartY=6.53806 StartZ=0 EndX=11.1059 EndY=6.51303 EndZ=0
    g131: LineSegment StartX=11.1059 StartY=6.51303 StartZ=0 EndX=12.2446 EndY=6.51303 EndZ=0
    g132: LineSegment StartX=12.2446 StartY=6.51303 StartZ=0 EndX=12.2446 EndY=6.04826 EndZ=0
    g133: BSplineCurve PolesCount=3 KnotsCount=2 Degree=2 IsPeriodic=0
    g134: BSplineCurve PolesCount=3 KnotsCount=2 Degree=2 IsPeriodic=0
    g135: BSplineCurve PolesCount=3 KnotsCount=2 Degree=2 IsPeriodic=0
    g136: BSplineCurve PolesCount=3 KnotsCount=2 Degree=2 IsPeriodic=0
    g137: BSplineCurve PolesCount=3 KnotsCount=2 Degree=2 IsPeriodic=0
    g138: BSplineCurve PolesCount=3 KnotsCount=2 Degree=2 IsPeriodic=0
    g139: BSplineCurve PolesCount=3 KnotsCount=2 Degree=2 IsPeriodic=0
    g140: BSplineCurve PolesCount=3 KnotsCount=2 Degree=2 IsPeriodic=0
    g141: BSplineCurve PolesCount=3 KnotsCount=2 Degree=2 IsPeriodic=0
    g142: BSplineCurve PolesCount=3 KnotsCount=2 Degree=2 IsPeriodic=0
    g143: BSplineCurve PolesCount=3 KnotsCount=2 Degree=2 IsPeriodic=0
    g144: LineSegment StartX=15.1941 StartY=8.66528 StartZ=0 EndX=15.1941 EndY=8.22375 EndZ=0
    g145: BSplineCurve PolesCount=3 KnotsCount=2 Degree=2 IsPeriodic=0
    g146: BSplineCurve PolesCount=3 KnotsCount=2 Degree=2 IsPeriodic=0
    g147: BSplineCurve PolesCount=3 KnotsCount=2 Degree=2 IsPeriodic=0
    g148: BSplineCurve PolesCount=3 KnotsCount=2 Degree=2 IsPeriodic=0
    g149: LineSegment StartX=14.0411 StartY=7.44257 StartZ=0 EndX=14.0643 EndY=7.44257 EndZ=0
    g150: BSplineCurve PolesCount=3 KnotsCount=2 Degree=2 IsPeriodic=0
    g151: BSplineCurve PolesCount=3 KnotsCount=2 Degree=2 IsPeriodic=0
    g152: BSplineCurve PolesCount=3 KnotsCount=2 Degree=2 IsPeriodic=0
    g153: BSplineCurve PolesCount=3 KnotsCount=2 Degree=2 IsPeriodic=0
    g154: BSplineCurve PolesCount=3 KnotsCount=2 Degree=2 IsPeriodic=0
    g155: BSplineCurve PolesCount=3 KnotsCount=2 Degree=2 IsPeriodic=0
    g156: BSplineCurve PolesCount=3 KnotsCount=2 Degree=2 IsPeriodic=0
    g157: BSplineCurve PolesCount=3 KnotsCount=2 Degree=2 IsPeriodic=0
    g158: BSplineCurve PolesCount=3 KnotsCount=2 Degree=2 IsPeriodic=0
    g159: BSplineCurve PolesCount=3 KnotsCount=2 Degree=2 IsPeriodic=0
    g160: BSplineCurve PolesCount=3 KnotsCount=2 Degree=2 IsPeriodic=0
    g161: BSplineCurve PolesCount=3 KnotsCount=2 Degree=2 IsPeriodic=0
    g162: BSplineCurve PolesCount=3 KnotsCount=2 Degree=2 IsPeriodic=0
    g163: BSplineCurve PolesCount=3 KnotsCount=2 Degree=2 IsPeriodic=0
    g164: BSplineCurve PolesCount=3 KnotsCount=2 Degree=2 IsPeriodic=0
    g165: BSplineCurve PolesCount=3 KnotsCount=2 Degree=2 IsPeriodic=0
    g166: LineSegment StartX=17.5697 StartY=6.04826 StartZ=0 EndX=17.0245 EndY=6.04826 EndZ=0
    g167: LineSegment StartX=17.0245 StartY=6.04826 StartZ=0 EndX=17.0245 EndY=7.21555 EndZ=0
    g168: BSplineCurve PolesCount=3 KnotsCount=2 Degree=2 IsPeriodic=0
    g169: BSplineCurve PolesCount=3 KnotsCount=2 Degree=2 IsPeriodic=0
    g170: BSplineCurve PolesCount=3 KnotsCount=2 Degree=2 IsPeriodic=0
    g171: BSplineCurve PolesCount=3 KnotsCount=2 Degree=2 IsPeriodic=0
    g172: LineSegment StartX=16.3256 StartY=6.98853 StartZ=0 EndX=16.3256 EndY=6.04826 EndZ=0
    g173: LineSegment StartX=16.3256 StartY=6.04826 StartZ=0 EndX=15.7804 EndY=6.04826 EndZ=0
    g174: LineSegment StartX=15.7804 StartY=6.04826 StartZ=0 EndX=15.7804 EndY=8.04678 EndZ=0
    g175: LineSegment StartX=15.7804 StartY=8.04678 StartZ=0 EndX=16.1969 EndY=8.04678 EndZ=0
    g176: LineSegment StartX=16.1969 StartY=8.04678 StartZ=0 EndX=16.2702 EndY=7.79115 EndZ=0
    g177: LineSegment StartX=16.2702 StartY=7.79115 StartZ=0 EndX=16.3006 EndY=7.79115 EndZ=0
    g178: BSplineCurve PolesCount=3 KnotsCount=2 Degree=2 IsPeriodic=0
    g179: BSplineCurve PolesCount=3 KnotsCount=2 Degree=2 IsPeriodic=0
    g180: BSplineCurve PolesCount=3 KnotsCount=2 Degree=2 IsPeriodic=0
    g181: LineSegment StartX=17.4893 StartY=7.79115 StartZ=0 EndX=17.5376 EndY=7.79115 EndZ=0
    g182: BSplineCurve PolesCount=3 KnotsCount=2 Degree=2 IsPeriodic=0
    g183: BSplineCurve PolesCount=3 KnotsCount=2 Degree=2 IsPeriodic=0
    g184: BSplineCurve PolesCount=3 KnotsCount=2 Degree=2 IsPeriodic=0
    g185: BSplineCurve PolesCount=3 KnotsCount=2 Degree=2 IsPeriodic=0
    g186: LineSegment StartX=18.8157 StartY=7.35141 StartZ=0 EndX=18.8157 EndY=6.04826 EndZ=0
    g187: LineSegment StartX=18.8157 StartY=6.04826 StartZ=0 EndX=18.2687 EndY=6.04826 EndZ=0
    g188: LineSegment StartX=18.2687 StartY=6.04826 StartZ=0 EndX=18.2687 EndY=7.21555 EndZ=0
    g189: BSplineCurve PolesCount=3 KnotsCount=2 Degree=2 IsPeriodic=0
    g190: BSplineCurve PolesCount=3 KnotsCount=2 Degree=2 IsPeriodic=0
    g191: BSplineCurve PolesCount=3 KnotsCount=2 Degree=2 IsPeriodic=0
    g192: BSplineCurve PolesCount=3 KnotsCount=2 Degree=2 IsPeriodic=0
    g193: LineSegment StartX=17.5697 StartY=7.0511 StartZ=0 EndX=17.5697 EndY=6.04826 EndZ=0
    g194: LineSegment StartX=21.1646 StartY=6.04826 StartZ=0 EndX=20.6193 EndY=6.04826 EndZ=0
    g195: LineSegment StartX=20.6193 StartY=6.04826 StartZ=0 EndX=20.6193 EndY=7.21555 EndZ=0
    g196: BSplineCurve PolesCount=3 KnotsCount=2 Degree=2 IsPeriodic=0
    g197: BSplineCurve PolesCount=3 KnotsCount=2 Degree=2 IsPeriodic=0
    g198: BSplineCurve PolesCount=3 KnotsCount=2 Degree=2 IsPeriodic=0
    g199: BSplineCurve PolesCount=3 KnotsCount=2 Degree=2 IsPeriodic=0
    g200: LineSegment StartX=19.9204 StartY=6.98853 StartZ=0 EndX=19.9204 EndY=6.04826 EndZ=0
    g201: LineSegment StartX=19.9204 StartY=6.04826 StartZ=0 EndX=19.3752 EndY=6.04826 EndZ=0
    g202: LineSegment StartX=19.3752 StartY=6.04826 StartZ=0 EndX=19.3752 EndY=8.04678 EndZ=0
    g203: LineSegment StartX=19.3752 StartY=8.04678 StartZ=0 EndX=19.7917 EndY=8.04678 EndZ=0
    g204: LineSegment StartX=19.7917 StartY=8.04678 StartZ=0 EndX=19.865 EndY=7.79115 EndZ=0
    g205: LineSegment StartX=19.865 StartY=7.79115 StartZ=0 EndX=19.8954 EndY=7.79115 EndZ=0
    g206: BSplineCurve PolesCount=3 KnotsCount=2 Degree=2 IsPeriodic=0
    g207: BSplineCurve PolesCount=3 KnotsCount=2 Degree=2 IsPeriodic=0
    g208: BSplineCurve PolesCount=3 KnotsCount=2 Degree=2 IsPeriodic=0
    g209: LineSegment StartX=21.0841 StartY=7.79115 StartZ=0 EndX=21.1324 EndY=7.79115 EndZ=0
    g210: BSplineCurve PolesCount=3 KnotsCount=2 Degree=2 IsPeriodic=0
    g211: BSplineCurve PolesCount=3 KnotsCount=2 Degree=2 IsPeriodic=0
    g212: BSplineCurve PolesCount=3 KnotsCount=2 Degree=2 IsPeriodic=0
    g213: BSplineCurve PolesCount=3 KnotsCount=2 Degree=2 IsPeriodic=0
    g214: LineSegment StartX=22.4105 StartY=7.35141 StartZ=0 EndX=22.4105 EndY=6.04826 EndZ=0
    g215: LineSegment StartX=22.4105 StartY=6.04826 StartZ=0 EndX=21.8635 EndY=6.04826 EndZ=0
    g216: LineSegment StartX=21.8635 StartY=6.04826 StartZ=0 EndX=21.8635 EndY=7.21555 EndZ=0
    g217: BSplineCurve PolesCount=3 KnotsCount=2 Degree=2 IsPeriodic=0
    g218: BSplineCurve PolesCount=3 KnotsCount=2 Degree=2 IsPeriodic=0
    g219: BSplineCurve PolesCount=3 KnotsCount=2 Degree=2 IsPeriodic=0
    g220: BSplineCurve PolesCount=3 KnotsCount=2 Degree=2 IsPeriodic=0
    g221: LineSegment StartX=21.1646 StartY=7.0511 StartZ=0 EndX=21.1646 EndY=6.04826 EndZ=0
  constraints (9):
    c: Horizontal(g0)
    c: Horizontal(g1)
    c: DistanceX(g1,g1) = 12
    c: DistanceX(g0,g0) = 12
    c: DistanceY(g-1,g-3) = 15
    c: DistanceY(g0,g-3) = 9
    c: DistanceY(g1,g-3) = 9
    c: T21(g0,g2,g3)
    c: T21(g1,g109,g110)
FEATURE [PartDesign::Pocket] Pocket001
  BaseFeature = -> Fillet
  Direction = (0,-1,2e-16)
  FuzzyTolerance = 0
  Length = 1
  Length2 = 5
  Profile = -> Sketch002
  ReferenceAxis = -> Sketch002 [N_Axis]
  Refine = true
  SideType = 0
  Suppressed = false
  Type = 0
  Type2 = 0
FEATURE [PartDesign::Body] Body
  AllowCompound = false
  Group = -> [Sketch,Pad,Sketch001,Pocket,Chamfer,Fillet,Sketch002,Pocket001]
  Origin = -> Origin
  Tip = -> Pocket001
